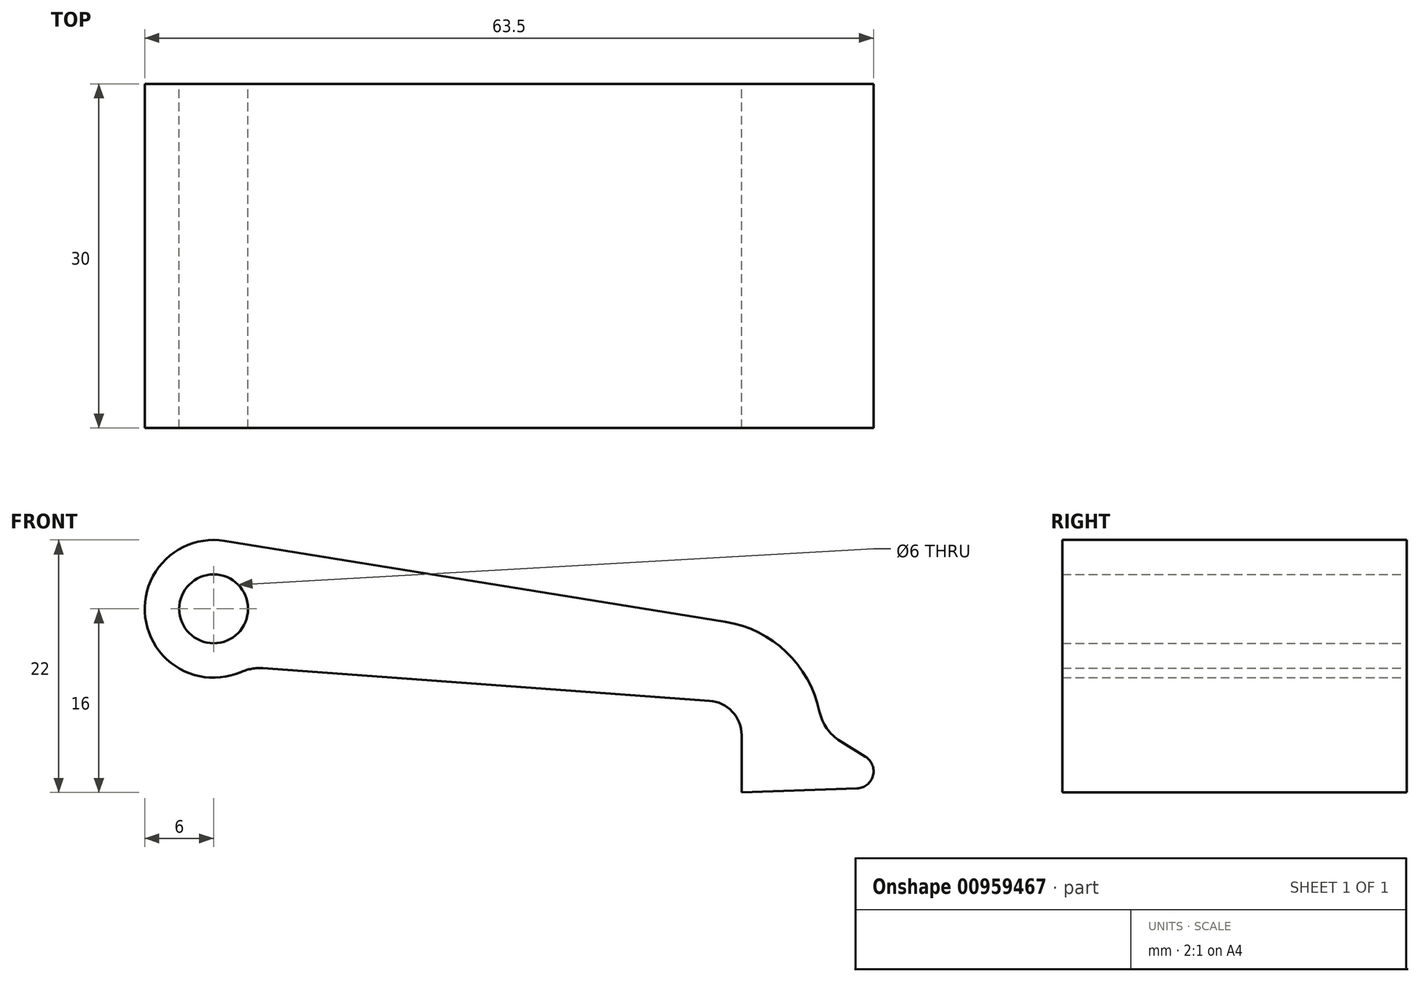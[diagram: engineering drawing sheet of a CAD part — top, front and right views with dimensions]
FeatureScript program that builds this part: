
annotation { "Feature Type Name" : "Feature", "Feature Type Description" : "" }
export const myFeature = defineFeature(function(context is Context, id is Id, definition is map)
    precondition{}
    {
        {
            var Q0;
            Q0=qCreatedBy(makeId("Front.planeOp"),FACE);
            var sketch = newSketch(context, id + "F0", { "sketchPlane" : qUnion([Q0])});
            skLineSegment(sketch, "E0", {"start": v(46, -11) * mm, "end": v(46, -16) * mm});
            skLineSegment(sketch, "E1", {"start": v(46, -16) * mm, "end": v(56.05, -15.65) * mm});
            skLineSegment(sketch, "E2", {"start": v(56.79, -12.87) * mm, "end": v(54.6, -11.51) * mm});
            skPoint(sketch, "E3.visualSharp", {"position": v(46, -7.07) * mm});
            skArc(sketch, "E3.filletArc", {"start": v(46, -11) * mm, "mid": v(45.2, -8.96) * mm, "end": v(43.22, -8) * mm});
            skPoint(sketch, "E4.visualSharp", {"position": v(6, 0) * mm});
            skPoint(sketch, "E5.visualSharp", {"position": v(49.03, -8.07) * mm});
            skArc(sketch, "E5.filletArc", {"start": v(52.79, -8.94) * mm, "mid": v(49.9, -3.76) * mm, "end": v(44.6, -1.13) * mm});
            skCircle(sketch, "E6", {"center": v(0, 0) * mm, "radius": 3 * mm});
            skLineSegment(sketch, "E7", {"start": v(0.96, 5.92) * mm, "end": v(44.6, -1.13) * mm});
            skLineSegment(sketch, "E8", {"start": v(4.3, -5.18) * mm, "end": v(43.22, -8) * mm});
            skArc(sketch, "E9", {"start": v(0.96, 5.92) * mm, "mid": v(-5.95, -0.75) * mm, "end": v(2.4, -5.5) * mm});
            skPoint(sketch, "E10.visualSharp", {"position": v(3.17, -5.1) * mm});
            skArc(sketch, "E10.filletArc", {"start": v(4.3, -5.18) * mm, "mid": v(3.33, -5.22) * mm, "end": v(2.4, -5.5) * mm});
            skPoint(sketch, "E11.visualSharp", {"position": v(52.99, -10.52) * mm});
            skArc(sketch, "E11.filletArc", {"start": v(52.79, -8.94) * mm, "mid": v(53.43, -10.41) * mm, "end": v(54.6, -11.51) * mm});
            skPoint(sketch, "E12.visualSharp", {"position": v(61, -15.48) * mm});
            skArc(sketch, "E12.filletArc", {"start": v(56.05, -15.65) * mm, "mid": v(57.45, -14.54) * mm, "end": v(56.79, -12.87) * mm});
            skSolve(sketch);
        }
        {
            var Q0;
            Q0 = qSketchRegion(id + "F0", true);
            extrude(context, id + "F1", {"entities" : qUnion([Q0]), "depth" : 30 * mm, "offsetDistance" : 25 * mm});
        }
    });
